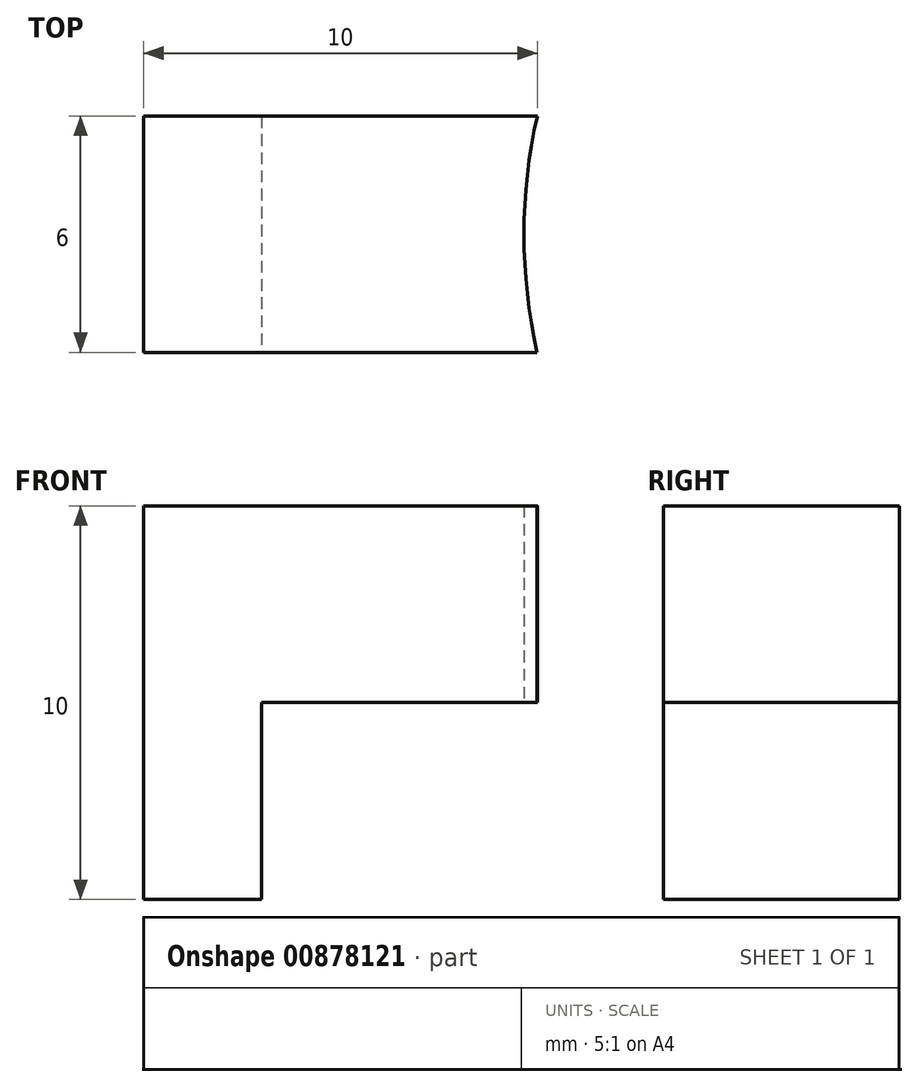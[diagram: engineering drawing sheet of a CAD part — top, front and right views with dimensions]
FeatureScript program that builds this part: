
annotation { "Feature Type Name" : "Feature", "Feature Type Description" : "" }
export const myFeature = defineFeature(function(context is Context, id is Id, definition is map)
    precondition{}
    {
        {
            var Q0;
            Q0=qCreatedBy(makeId("Top.planeOp"),FACE);
            var sketch = newSketch(context, id + "F0", { "sketchPlane" : qUnion([Q0])});
            skLineSegment(sketch, "E0", {"start": v(10, 6) * mm, "end": v(0, 6) * mm});
            skLineSegment(sketch, "E1", {"start": v(0, 6) * mm, "end": v(0, 0) * mm});
            skLineSegment(sketch, "E2", {"start": v(0, 0) * mm, "end": v(10, 0) * mm});
            skArc(sketch, "E3.0", {"start": v(10, 6) * mm, "mid": v(9.66, 3) * mm, "end": v(10, 0) * mm});
            skSolve(sketch);
        }
        {
            var Q0;
            Q0 = qSketchRegion(id + "F0", true);
            extrude(context, id + "F1", {"entities" : qUnion([Q0]), "depth" : 5 * mm, "offsetDistance" : 25 * mm});
        }
        {
            var Q0;
            Q0=makeQuery(id+"F1.opExtrude","SWEPT_FACE",FACE,{"disambiguationData":[OSD([sQuery(id+"F0.wireOp",EDGE,"E2")])]});
            var sketch = newSketch(context, id + "F2", { "sketchPlane" : qUnion([Q0])});
            skLineSegment(sketch, "E4", {"start": v(0, 0) * mm, "end": v(0, -5) * mm});
            skLineSegment(sketch, "E5", {"start": v(0, -5) * mm, "end": v(3, -5) * mm});
            skLineSegment(sketch, "E6", {"start": v(3, -5) * mm, "end": v(3, 0) * mm});
            skSolve(sketch);
        }
        {
            var Q0;
            {var subQ0=sQuery(id+"F2.wireOp",EDGE,"E4");Q0=makeQuery(id+"F2.imprint","IMPRINT",FACE,{"disambiguationData":[TD([[makeQuery(id+"F2.imprint","IMPRINT",EDGE,{"derivedFrom":subQ0}),1.0]])]});}
            extrude(context, id + "F3", {"entities" : qUnion([Q0]), "operationType" : NewBodyOperationType.ADD, "oppositeDirection" : true, "depth" : 6 * mm, "offsetDistance" : 25 * mm});
        }
    });
